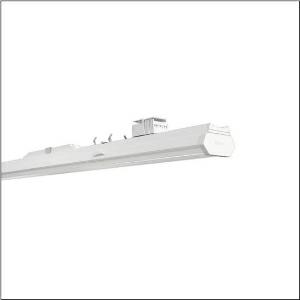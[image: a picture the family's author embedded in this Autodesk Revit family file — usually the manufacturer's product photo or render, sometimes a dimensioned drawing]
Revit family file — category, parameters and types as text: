
# Revit family: licross_r__21_protected_mo_52td1bvn48xg_aeae
name_source: partatom
category: Lighting Fixtures
units: mm (PartAtom-declared; Revit-internal decimal feet)

## family parameters
Cut with Voids When Loaded = No
Host = Face
Light Source = No
Part Type = Normal
Room Calculation Point = No
Round Connector Dimension = Use Diameter
Shared = No

## types (1)
- --- (1 x LED, 8000 lm, 48.3 W, 4000K)
    Apparent Load = 48 VA
    CIE Flux Codes = 54 82 95 97 100
    Color Rendering = 80
    Color Temperature = 4000K
    Default Elevation = 1800 mm
    Description = Licross® 21 Protected MO, luminaire insert, of sheet steel, galvanised, coil coated, white, length: 1.500mm, width: 90mm, height: 101mm, LED rated luminous flux: 8.000lm, light colour: 840, control gear: DALI 2, CLO, with plug, 5-pole, with phase selection, mains connection: 220..240V, AC, 50/60Hz, start of lifetime: 48W, end of service life: 58W, internal wiring halogen-free, primary optical cover: cover, of PMMA, light emission: direct distribution, primary light characteristic: symmetric, protection rating (complete): IP54, insulation class (complete): insulation class I (protective earthing), certification: CE, ENEC, VDE, UKCA, protection symbol: D if used in an environment with non-conductive dust loads with corresponding accessories, impact resistance: IK06, permissible ambient temperature for indoor applications: -25..+40°C, corresponds to IFS (International Featured Standards) requirements for safety and quality in the food industry, reducing of maximum allowable ambient temperature of 5°C with ceiling mounting, LABS conformity tested according to VDMA 24364:2018-05, packaging unit: 1 piece
    Height = 92 mm
    Lamp = 1 x LED
    Lamp Light Flux = 8000 lm
    Lamp Power = 48.3 W
    Lamp count = 1
    Length = 1500 mm
    Luminous efficacy = 166 lm/W
    Manufacturer = Siteco
    ModVariant = No
    Model = 52TD1BVN48XG
    Mounting Place = Ceiling
    Mounting Type = Pendant
    Number of Poles = 1
    OnlyDefault = Yes
    Power Factor = 1
    Product Name = Licross® 21 Protected MO
    Product group = luminaire insert | ceiling pendant
    ProductGroupID = 902
    Protection Class = Protection class I
    Protection Degree = IP 54
    RLX_Detail_Level = 1
    RLX_Emergency_Light_Flux = 0 lm
    RLX_Emergency_Type = 0
    RLX_Emergency_Type_DB = No
    RlxData = <blob elided: 24493 chars, md5=af1d9395>
    Socket = socket
    Standby Power = 0 W
    System Light Flux = 8000 lm
    System Power = 48 W
    Type Comments = factory setting: luminous flux: 100 % | dim-lin: 254 | 326 mA
    Type Image = l_1256148.jpg
    URL = http://relux.com
    VarID = @adj_104381
    Voltage = 0 V
    Weight = 0.00 kg
    Width = 88 mm

## geometry (parser evidence)
native form markers: Blend x4, Sweep x11
no freeform markers — native parametric forms only
